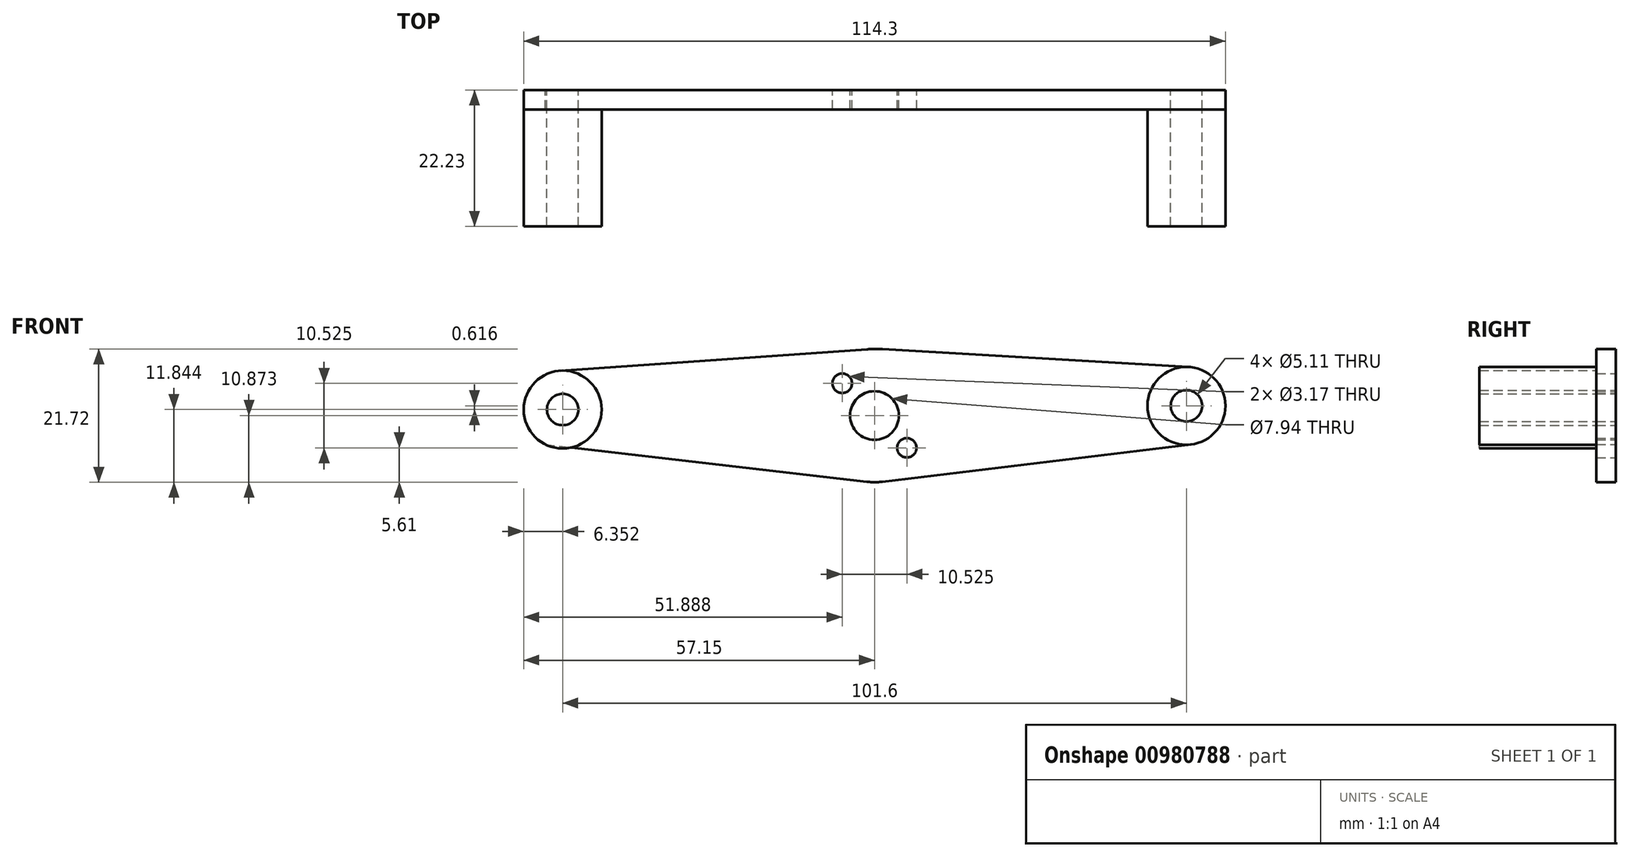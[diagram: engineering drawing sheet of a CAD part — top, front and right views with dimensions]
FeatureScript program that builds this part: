
annotation { "Feature Type Name" : "Feature", "Feature Type Description" : "" }
export const myFeature = defineFeature(function(context is Context, id is Id, definition is map)
    precondition{}
    {
        {
            var Q0;
            Q0=qCreatedBy(makeId("Front.planeOp"),FACE);
            var sketch = newSketch(context, id + "F0", { "sketchPlane" : qUnion([Q0])});
            skCircle(sketch, "E0", {"center": v(-50.8, -0.62) * mm, "radius": 2.55 * mm});
            skCircle(sketch, "E1", {"center": v(50.8, 0) * mm, "radius": 2.55 * mm});
            skCircle(sketch, "E2", {"center": v(-50.8, -0.62) * mm, "radius": 6.35 * mm, "construction": true});
            skCircle(sketch, "E3", {"center": v(50.8, 0) * mm, "radius": 6.35 * mm, "construction": true});
            skArc(sketch, "E4", {"start": v(-51.24, 5.72) * mm, "mid": v(-57.03, 0.62) * mm, "end": v(-53.62, -6.3) * mm});
            skArc(sketch, "E5", {"start": v(51.17, 6.34) * mm, "mid": v(57.15, 0.2) * mm, "end": v(51.56, -6.3) * mm});
            skLineSegment(sketch, "E6", {"start": v(51.56, -6.3) * mm, "end": v(1.3, -12.38) * mm});
            skLineSegment(sketch, "E7", {"start": v(51.17, 6.34) * mm, "end": v(1.3, 9.23) * mm});
            skArc(sketch, "E8", {"start": v(-1.25, -12.39) * mm, "mid": v(0.03, -12.46) * mm, "end": v(1.3, -12.38) * mm});
            skArc(sketch, "E9", {"start": v(1.3, 9.23) * mm, "mid": v(0.03, 9.26) * mm, "end": v(-1.25, 9.21) * mm});
            skLineSegment(sketch, "E10", {"start": v(-51.24, 5.72) * mm, "end": v(-1.25, 9.21) * mm});
            skLineSegment(sketch, "E11", {"start": v(-53.62, -6.3) * mm, "end": v(-1.25, -12.39) * mm});
            skLineSegment(sketch, "E12", {"start": v(-5.26, 3.67) * mm, "end": v(0, -1.59) * mm, "construction": true});
            skLineSegment(sketch, "E13", {"start": v(0, -1.59) * mm, "end": v(5.26, -6.85) * mm, "construction": true});
            skCircle(sketch, "E14", {"center": v(5.26, -6.85) * mm, "radius": 1.59 * mm});
            skCircle(sketch, "E15", {"center": v(-5.26, 3.67) * mm, "radius": 1.59 * mm});
            skCircle(sketch, "E16", {"center": v(0, -1.59) * mm, "radius": 3.97 * mm});
            skCircle(sketch, "E17", {"center": v(0, -1.59) * mm, "radius": 10.87 * mm, "construction": true});
            skLineSegment(sketch, "E18", {"start": v(50.8, 0) * mm, "end": v(0, 0) * mm, "construction": true});
            skLineSegment(sketch, "E19", {"start": v(-50.8, -0.62) * mm, "end": v(0, 0) * mm, "construction": true});
            skSolve(sketch);
        }
        {
            var Q0;
            Q0 = qSketchRegion(id + "F0", true);
            extrude(context, id + "F1", {"entities" : qUnion([Q0]), "depth" : 3.17 * mm, "offsetDistance" : 25.4 * mm});
        }
        {
            var Q0;
            Q0=makeQuery(id+"F1.opExtrude","CAP_FACE",FACE,{"disambiguationData":[OSD([sQuery(id+"F0.wireOp",EDGE,"E0"),sQuery(id+"F0.wireOp",EDGE,"E1"),sQuery(id+"F0.wireOp",EDGE,"E4"),sQuery(id+"F0.wireOp",EDGE,"E5"),sQuery(id+"F0.wireOp",EDGE,"E6"),sQuery(id+"F0.wireOp",EDGE,"E7"),sQuery(id+"F0.wireOp",EDGE,"E8"),sQuery(id+"F0.wireOp",EDGE,"E9"),sQuery(id+"F0.wireOp",EDGE,"E10"),sQuery(id+"F0.wireOp",EDGE,"E11"),sQuery(id+"F0.wireOp",EDGE,"E14"),sQuery(id+"F0.wireOp",EDGE,"E15"),sQuery(id+"F0.wireOp",EDGE,"E16")])],"isStart":false});
            var sketch = newSketch(context, id + "F2", { "sketchPlane" : qUnion([Q0])});
            skCircle(sketch, "E20", {"center": v(-50.8, -0.62) * mm, "radius": 6.35 * mm});
            skCircle(sketch, "E21", {"center": v(50.8, 0) * mm, "radius": 6.35 * mm});
            skCircle(sketch, "E22", {"center": v(-50.8, -0.62) * mm, "radius": 2.55 * mm});
            skCircle(sketch, "E23", {"center": v(50.8, 0) * mm, "radius": 2.55 * mm});
            skSolve(sketch);
        }
        {
            var Q0;
            Q0 = qSketchRegion(id + "F2", true);
            extrude(context, id + "F3", {"entities" : qUnion([Q0]), "depth" : 19.05 * mm, "offsetDistance" : 25.4 * mm});
        }
    });
